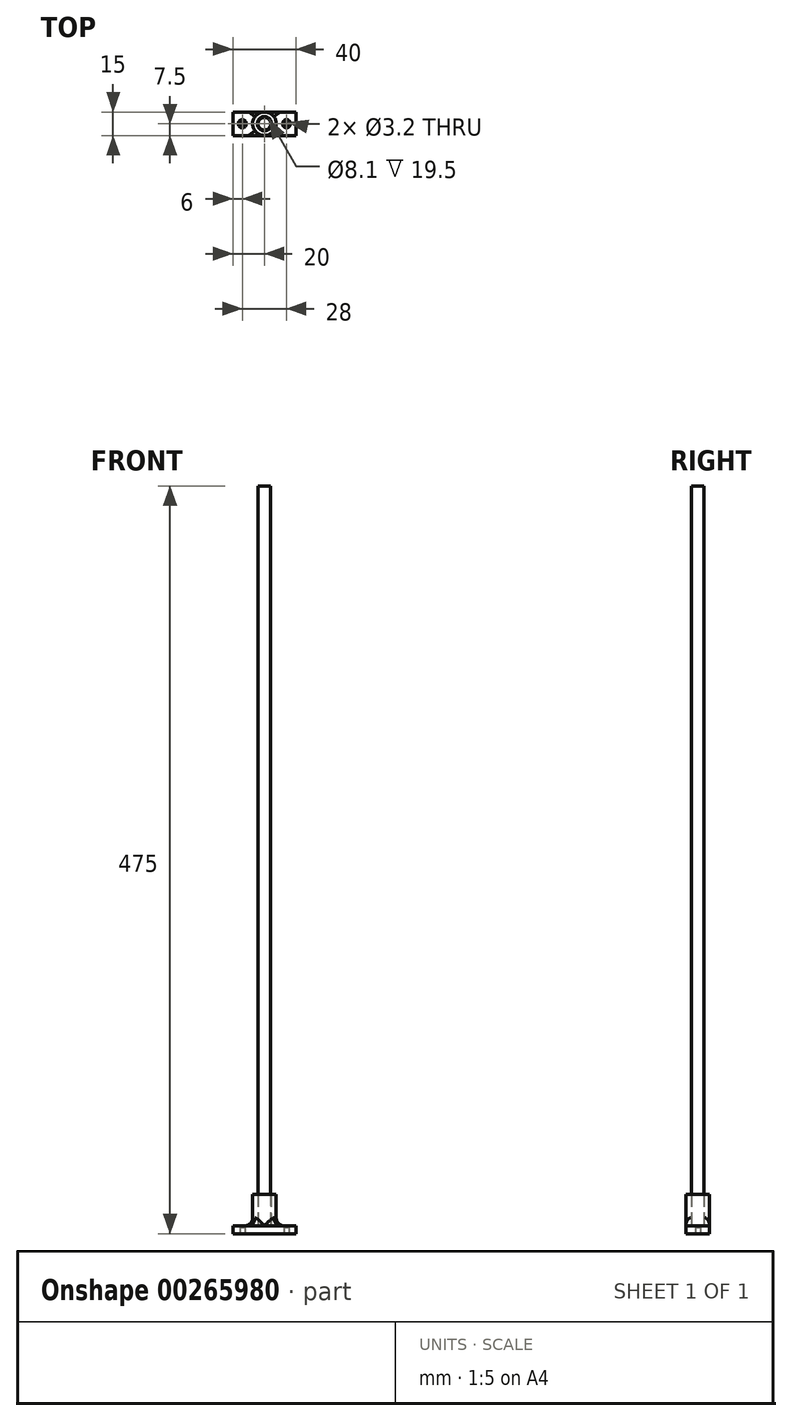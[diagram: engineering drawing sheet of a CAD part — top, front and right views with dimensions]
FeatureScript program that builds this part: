
annotation { "Feature Type Name" : "Feature", "Feature Type Description" : "" }
export const myFeature = defineFeature(function(context is Context, id is Id, definition is map)
    precondition{}
    {
        {
            var Q0;
            Q0=qCreatedBy(makeId("Top.planeOp"),FACE);
            var sketch = newSketch(context, id + "F0", { "sketchPlane" : qUnion([Q0])});
            skLineSegment(sketch, "E0.bottom", {"start": v(0, 0) * mm, "end": v(40, 0) * mm});
            skLineSegment(sketch, "E0.top", {"start": v(0, 15) * mm, "end": v(40, 15) * mm});
            skLineSegment(sketch, "E0.left", {"start": v(0, 0) * mm, "end": v(0, 15) * mm});
            skLineSegment(sketch, "E0.right", {"start": v(40, 0) * mm, "end": v(40, 15) * mm});
            skSolve(sketch);
        }
        {
            var Q0;
            Q0=makeQuery(id+"F0.imprint","IMPRINT",FACE,{"disambiguationData":[TD([[makeQuery(id+"F0.imprint","IMPRINT",EDGE,{"derivedFrom":sQuery(id+"F0.wireOp",EDGE,"E0.bottom")}),1.0]])]});
            extrude(context, id + "F1", {"entities" : qUnion([Q0]), "depth" : 4 * mm});
        }
        {
            var Q0;
            Q0=makeQuery(id+"F1.opExtrude","CAP_FACE",FACE,{"disambiguationData":[OSD([sQuery(id+"F0.wireOp",EDGE,"E0.bottom"),sQuery(id+"F0.wireOp",EDGE,"E0.top"),sQuery(id+"F0.wireOp",EDGE,"E0.left"),sQuery(id+"F0.wireOp",EDGE,"E0.right")])],"isStart":false});
            var sketch = newSketch(context, id + "F2", { "sketchPlane" : qUnion([Q0])});
            skCircle(sketch, "E1", {"center": v(20, 7.5) * mm, "radius": 4.05 * mm});
            skCircle(sketch, "E2", {"center": v(20, 7.5) * mm, "radius": 7.5 * mm});
            skSolve(sketch);
        }
        {
            var Q0;
            Q0=makeQuery(id+"F2.imprint","IMPRINT",FACE,{"disambiguationData":[TD([[makeQuery(id+"F2.imprint","IMPRINT",EDGE,{"derivedFrom":sQuery(id+"F2.wireOp",EDGE,"E1")}),-1.0]])]});
            extrude(context, id + "F3", {"entities" : qUnion([Q0]), "operationType" : NewBodyOperationType.ADD, "depth" : 20 * mm});
        }
        {
            var Q0;
            Q0=makeQuery(id+"F3.boolean.opBoolean","SPLIT",EDGE,{"disambiguationData":[OD(0.0)],"derivedFrom":makeQuery(id+"F3.opExtrude","CAP_EDGE",EDGE,{"disambiguationData":[OSD([sQuery(id+"F2.wireOp",EDGE,"E2")])],"isStart":true})});
            fillet(context, id + "F4", {"entities" : qUnion([Q0]), "radius" : 5 * mm, "tangentPropagation" : true, "allowEdgeOverflow" : false});
        }
        {
            var Q0;
            Q0=makeQuery(id+"F1.opExtrude","CAP_FACE",FACE,{"disambiguationData":[OSD([sQuery(id+"F0.wireOp",EDGE,"E0.bottom"),sQuery(id+"F0.wireOp",EDGE,"E0.top"),sQuery(id+"F0.wireOp",EDGE,"E0.left"),sQuery(id+"F0.wireOp",EDGE,"E0.right")])],"isStart":true});
            var sketch = newSketch(context, id + "F5", { "sketchPlane" : qUnion([Q0])});
            skCircle(sketch, "E3", {"center": v(6, -7.5) * mm, "radius": 1.6 * mm});
            skPoint(sketch, "E3.centerSnap0", {"position": v(0, -7.5) * mm});
            skCircle(sketch, "E4", {"center": v(34, -7.5) * mm, "radius": 1.6 * mm});
            skPoint(sketch, "E4.centerSnap0", {"position": v(40, -7.5) * mm});
            skSolve(sketch);
        }
        {
            var Q0;
            Q0=makeQuery(id+"F5.imprint","IMPRINT",FACE,{"disambiguationData":[TD([[makeQuery(id+"F5.imprint","IMPRINT",EDGE,{"derivedFrom":sQuery(id+"F5.wireOp",EDGE,"E3")}),1.0]])]});
            var Q1;
            Q1=makeQuery(id+"F5.imprint","IMPRINT",FACE,{"disambiguationData":[TD([[makeQuery(id+"F5.imprint","IMPRINT",EDGE,{"derivedFrom":sQuery(id+"F5.wireOp",EDGE,"E4")}),1.0]])]});
            extrude(context, id + "F6", {"entities" : qUnion([Q0, Q1]), "operationType" : NewBodyOperationType.REMOVE, "oppositeDirection" : true, "depth" : 25 * mm});
        }
        {
            var Q0;
            {var subQ0=sQuery(id+"F0.wireOp",EDGE,"E0.left");var subQ1=sQuery(id+"F0.wireOp",EDGE,"E0.top");var subQ2=sQuery(id+"F0.wireOp",EDGE,"E0.bottom");var subQ3=makeQuery(id+"F1.opExtrude","CAP_FACE",FACE,{"disambiguationData":[OSD([subQ2,subQ1,subQ0,sQuery(id+"F0.wireOp",EDGE,"E0.right")])],"isStart":false});Q0=makeQuery(id+"F6.boolean.opBoolean","INTERSECT",EDGE,{"derivedFrom":[makeQuery(id+"F3.boolean.opBoolean","SPLIT",FACE,{"disambiguationData":[TD([makeQuery(id+"F1.opExtrude","SWEPT_FACE",FACE,{"disambiguationData":[OSD([subQ0])]})])],"derivedFrom":subQ3}),makeQuery(id+"F6.opExtrude","SWEPT_FACE",FACE,{"disambiguationData":[OSD([sQuery(id+"F5.wireOp",EDGE,"E3")])]})]});}
            var Q1;
            {var subQ0=sQuery(id+"F2.wireOp",EDGE,"E2");Q1=makeQuery(id+"F6.boolean.opBoolean","INTERSECT",EDGE,{"derivedFrom":[makeQuery(id+"F4.opFillet","BLEND_FACE",FACE,{"disambiguationData":[OSD([subQ0]),TDD([makeQuery(id+"F3.boolean.opBoolean","SPLIT",EDGE,{"disambiguationData":[OD(0.0)],"derivedFrom":makeQuery(id+"F3.opExtrude","CAP_EDGE",EDGE,{"disambiguationData":[OSD([subQ0])],"isStart":true})})]),OD(2.0)]}),makeQuery(id+"F6.opExtrude","SWEPT_FACE",FACE,{"disambiguationData":[OSD([sQuery(id+"F5.wireOp",EDGE,"E3")])]})]});}
            var Q2;
            {var subQ0=sQuery(id+"F0.wireOp",EDGE,"E0.top");var subQ1=sQuery(id+"F0.wireOp",EDGE,"E0.right");var subQ2=sQuery(id+"F0.wireOp",EDGE,"E0.bottom");var subQ3=makeQuery(id+"F1.opExtrude","CAP_FACE",FACE,{"disambiguationData":[OSD([subQ2,subQ0,sQuery(id+"F0.wireOp",EDGE,"E0.left"),subQ1])],"isStart":false});Q2=makeQuery(id+"F6.boolean.opBoolean","INTERSECT",EDGE,{"derivedFrom":[makeQuery(id+"F3.boolean.opBoolean","SPLIT",FACE,{"disambiguationData":[TD([makeQuery(id+"F1.opExtrude","SWEPT_FACE",FACE,{"disambiguationData":[OSD([subQ1])]})])],"derivedFrom":subQ3}),makeQuery(id+"F6.opExtrude","SWEPT_FACE",FACE,{"disambiguationData":[OSD([sQuery(id+"F5.wireOp",EDGE,"E4")])]})]});}
            var Q3;
            {var subQ0=sQuery(id+"F2.wireOp",EDGE,"E2");Q3=makeQuery(id+"F6.boolean.opBoolean","INTERSECT",EDGE,{"derivedFrom":[makeQuery(id+"F4.opFillet","BLEND_FACE",FACE,{"disambiguationData":[OSD([subQ0]),TDD([makeQuery(id+"F3.boolean.opBoolean","SPLIT",EDGE,{"disambiguationData":[OD(1.0)],"derivedFrom":makeQuery(id+"F3.opExtrude","CAP_EDGE",EDGE,{"disambiguationData":[OSD([subQ0])],"isStart":true})})]),OD(2.0)]}),makeQuery(id+"F6.opExtrude","SWEPT_FACE",FACE,{"disambiguationData":[OSD([sQuery(id+"F5.wireOp",EDGE,"E4")])]})]});}
            chamfer(context, id + "F7", {"entities" : qUnion([Q0, Q1, Q2, Q3]), "width" : 1 * mm, "tangentPropagation" : true});
        }
        {
            var Q0;
            Q0=makeQuery(id+"F1.opExtrude","CAP_FACE",FACE,{"disambiguationData":[OSD([sQuery(id+"F0.wireOp",EDGE,"E0.bottom"),sQuery(id+"F0.wireOp",EDGE,"E0.top"),sQuery(id+"F0.wireOp",EDGE,"E0.left"),sQuery(id+"F0.wireOp",EDGE,"E0.right")])],"isStart":true});
            extrude(context, id + "F8", {"entities" : qUnion([Q0]), "operationType" : NewBodyOperationType.ADD, "depth" : 1 * mm});
        }
        {
            var Q0;
            Q0=makeQuery(id+"F3.opExtrude","CAP_EDGE",EDGE,{"disambiguationData":[OSD([sQuery(id+"F2.wireOp",EDGE,"E1")])],"isStart":false});
            chamfer(context, id + "F9", {"entities" : qUnion([Q0]), "width" : .5 * mm, "tangentPropagation" : true});
        }
        {
            var Q0;
            Q0=makeQuery(id+"F3.boolean.opBoolean","SPLIT",FACE,{"disambiguationData":[TD([makeQuery(id+"F3.opExtrude","SWEPT_FACE",FACE,{"disambiguationData":[OSD([sQuery(id+"F2.wireOp",EDGE,"E1")])]})])],"derivedFrom":makeQuery(id+"F1.opExtrude","CAP_FACE",FACE,{"disambiguationData":[OSD([sQuery(id+"F0.wireOp",EDGE,"E0.bottom"),sQuery(id+"F0.wireOp",EDGE,"E0.top"),sQuery(id+"F0.wireOp",EDGE,"E0.left"),sQuery(id+"F0.wireOp",EDGE,"E0.right")])],"isStart":false})});
            var sketch = newSketch(context, id + "F10", { "sketchPlane" : qUnion([Q0])});
            skCircle(sketch, "E5", {"center": v(20, 7.5) * mm, "radius": 4 * mm});
            skSolve(sketch);
        }
        {
            var Q0;
            Q0=qSketchRegion(id+"F10",true);
            extrude(context, id + "F11", {"entities" : qUnion([Q0]), "depth" : 400 * mm});
        }
        {
            var Q0;
            Q0=makeQuery(id+"F11.opExtrude","CAP_FACE",FACE,{"disambiguationData":[OSD([sQuery(id+"F10.wireOp",EDGE,"E5")])],"isStart":false});
            extrude(context, id + "F12", {"entities" : qUnion([Q0]), "operationType" : NewBodyOperationType.ADD, "depth" : 70 * mm, "offsetDistance" : 25 * mm});
        }
    });
